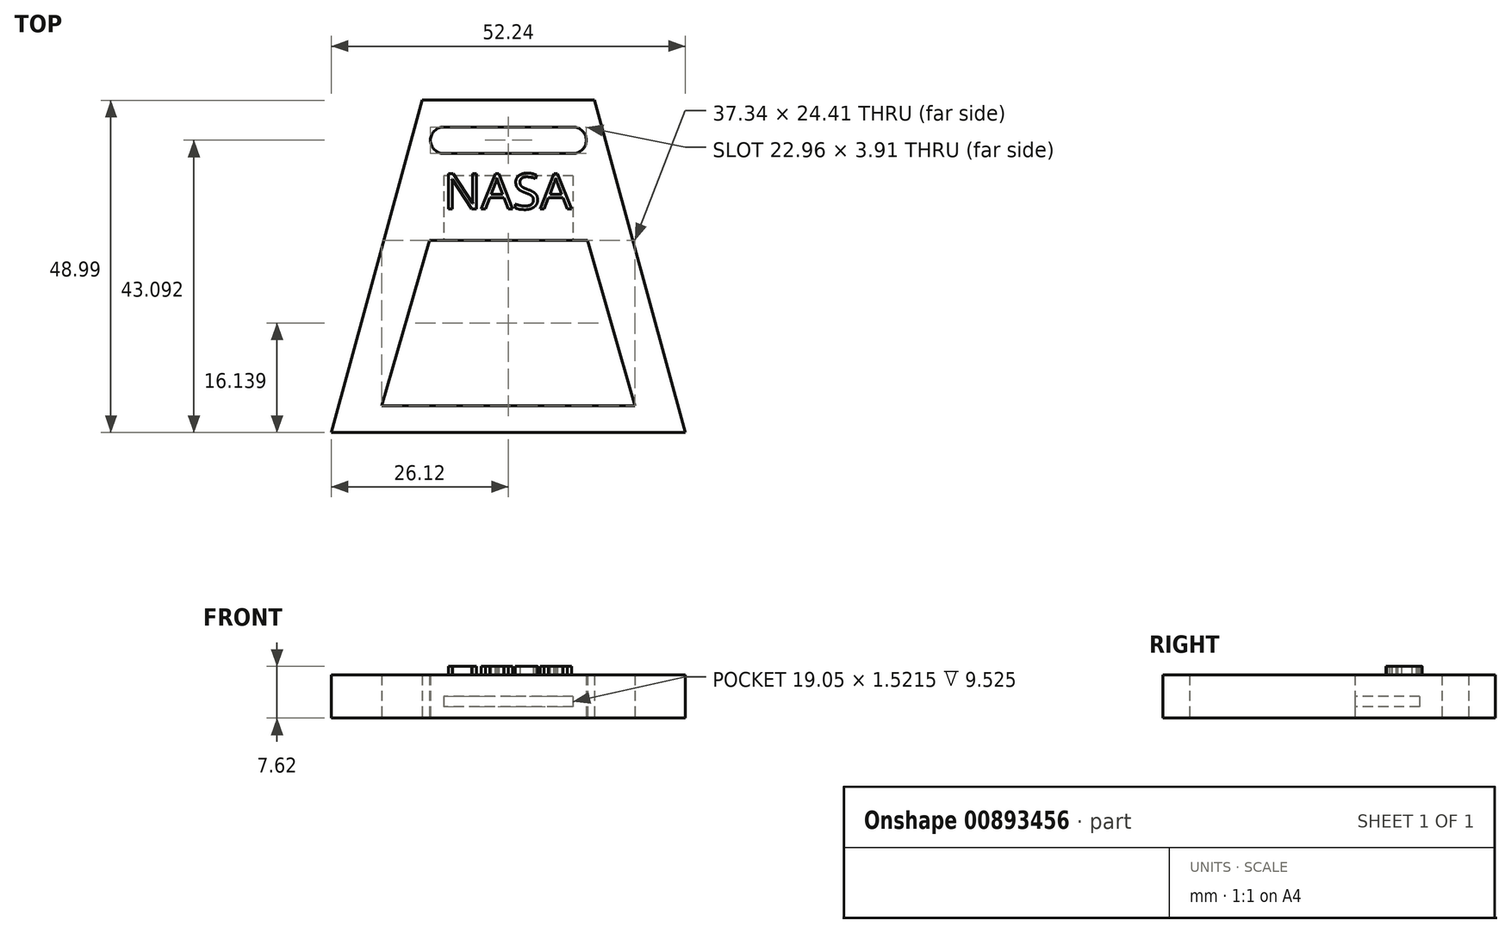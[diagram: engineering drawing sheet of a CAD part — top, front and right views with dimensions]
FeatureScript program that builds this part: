
annotation { "Feature Type Name" : "Feature", "Feature Type Description" : "" }
export const myFeature = defineFeature(function(context is Context, id is Id, definition is map)
    precondition{}
    {
        {
            var Q0;
            Q0=qCreatedBy(makeId("Top.planeOp"),FACE);
            var sketch = newSketch(context, id + "F0", { "sketchPlane" : qUnion([Q0])});
            skLineSegment(sketch, "E0", {"start": v(0, 29.12) * mm, "end": v(-12.7, 29.12) * mm});
            skLineSegment(sketch, "E1", {"start": v(-12.7, 29.12) * mm, "end": v(-26.12, -19.87) * mm});
            skLineSegment(sketch, "E2", {"start": v(-26.12, -19.87) * mm, "end": v(0, -19.87) * mm});
            skLineSegment(sketch, "E3", {"start": v(0, 25.18) * mm, "end": v(-9.53, 25.18) * mm});
            skLineSegment(sketch, "E4", {"start": v(0, 25.18) * mm, "end": v(0, 21.27) * mm});
            skLineSegment(sketch, "E5", {"start": v(0, 21.27) * mm, "end": v(-9.53, 21.27) * mm});
            skArc(sketch, "E6", {"start": v(-9.53, 25.18) * mm, "mid": v(-11.48, 23.22) * mm, "end": v(-9.53, 21.27) * mm});
            skLineSegment(sketch, "E7", {"start": v(-18.67, -15.94) * mm, "end": v(-11.66, 8.48) * mm});
            skLineSegment(sketch, "E8", {"start": v(-11.66, 8.48) * mm, "end": v(0, 8.48) * mm});
            skLineSegment(sketch, "E9", {"start": v(-11.66, 8.48) * mm, "end": v(-18.67, -15.94) * mm});
            skLineSegment(sketch, "E10", {"start": v(0, 8.48) * mm, "end": v(0, -15.94) * mm});
            skLineSegment(sketch, "E11", {"start": v(-18.67, -15.94) * mm, "end": v(0, -15.94) * mm});
            skLineSegment(sketch, "E12", {"start": v(0, -15.94) * mm, "end": v(0, -19.87) * mm});
            skLineSegment(sketch, "E13", {"start": v(0, 21.27) * mm, "end": v(0, 8.48) * mm});
            skLineSegment(sketch, "E14", {"start": v(0, 29.12) * mm, "end": v(0, 25.18) * mm});
            skSolve(sketch);
        }
        {
            var Q0;
            Q0=makeQuery(id+"F0.imprint","IMPRINT",FACE,{"disambiguationData":[TD([[makeQuery(id+"F0.imprint","IMPRINT",EDGE,{"derivedFrom":sQuery(id+"F0.wireOp",EDGE,"E0")}),1.0]])]});
            extrude(context, id + "F1", {"entities" : qUnion([Q0]), "depth" : 6.35 * mm, "offsetDistance" : 25.4 * mm});
        }
        {
            var Q0;
            Q0=makeQuery(id+"F1.opExtrude","SWEPT_FACE",FACE,{"disambiguationData":[OSD([sQuery(id+"F0.wireOp",EDGE,"E8")])]});
            var sketch = newSketch(context, id + "F2", { "sketchPlane" : qUnion([Q0])});
            skLineSegment(sketch, "E15", {"start": v(0, 1.65) * mm, "end": v(0, 3.18) * mm});
            skLineSegment(sketch, "E16", {"start": v(0, 3.18) * mm, "end": v(-9.53, 3.18) * mm});
            skLineSegment(sketch, "E17", {"start": v(0, 1.65) * mm, "end": v(-9.53, 1.65) * mm});
            skLineSegment(sketch, "E18", {"start": v(-9.53, 3.18) * mm, "end": v(-9.53, 1.65) * mm});
            skSolve(sketch);
        }
        {
            var Q0;
            Q0=makeQuery(id+"F2.imprint","IMPRINT",FACE,{"disambiguationData":[TD([[makeQuery(id+"F2.imprint","IMPRINT",EDGE,{"derivedFrom":sQuery(id+"F2.wireOp",EDGE,"E15")}),-1.0]])]});
            extrude(context, id + "F3", {"entities" : qUnion([Q0]), "operationType" : NewBodyOperationType.REMOVE, "oppositeDirection" : true, "depth" : 9.52 * mm, "offsetDistance" : 25.4 * mm});
        }
        {
            var Q0;
            Q0=makeQuery(id+"F1.opExtrude","SWEPT_BODY",BODY,{"disambiguationData":[OSD([sQuery(id+"F0.wireOp",EDGE,"E0"),sQuery(id+"F0.wireOp",EDGE,"E1"),sQuery(id+"F0.wireOp",EDGE,"E2"),sQuery(id+"F0.wireOp",EDGE,"E3"),sQuery(id+"F0.wireOp",EDGE,"E5"),sQuery(id+"F0.wireOp",EDGE,"E6"),sQuery(id+"F0.wireOp",EDGE,"E8"),sQuery(id+"F0.wireOp",EDGE,"E9"),sQuery(id+"F0.wireOp",EDGE,"E11"),sQuery(id+"F0.wireOp",EDGE,"E12"),sQuery(id+"F0.wireOp",EDGE,"E13"),sQuery(id+"F0.wireOp",EDGE,"E14")])]});
            var Q1;
            Q1=qCreatedBy(makeId("Right.planeOp"),FACE);
            mirror(context, id + "F4", {"operationType" : NewBodyOperationType.ADD, "entities" : qUnion([Q0]), "mirrorPlane" : qUnion([Q1])});
        }
        {
            var Q0;
            {var subQ0=makeQuery(id+"F1.opExtrude","CAP_FACE",FACE,{"disambiguationData":[OSD([sQuery(id+"F0.wireOp",EDGE,"E0"),sQuery(id+"F0.wireOp",EDGE,"E1"),sQuery(id+"F0.wireOp",EDGE,"E2"),sQuery(id+"F0.wireOp",EDGE,"E3"),sQuery(id+"F0.wireOp",EDGE,"E5"),sQuery(id+"F0.wireOp",EDGE,"E6"),sQuery(id+"F0.wireOp",EDGE,"E8"),sQuery(id+"F0.wireOp",EDGE,"E9"),sQuery(id+"F0.wireOp",EDGE,"E11"),sQuery(id+"F0.wireOp",EDGE,"E12"),sQuery(id+"F0.wireOp",EDGE,"E13"),sQuery(id+"F0.wireOp",EDGE,"E14")])],"isStart":false});Q0=makeQuery(id+"F4.boolean.opBoolean","MERGE",FACE,{"derivedFrom":[subQ0,makeQuery(id+"F4.opPattern","COPY",FACE,{"derivedFrom":subQ0,"instanceName":"1"})]});}
            var sketch = newSketch(context, id + "F5", { "sketchPlane" : qUnion([Q0])});
            skText(sketch, "E19", { "text": "NASA", "fontName": "OpenSans-Regular.ttf"});
            const initialGuessF5  = {"E19": [-0.00953, 0.01306, 1, 0, 0.00528]};
            skSetInitialGuess(sketch, initialGuessF5);
            skSolve(sketch);
        }
        {
            var Q0;
            Q0 = qSketchRegion(id + "F5", true);
            extrude(context, id + "F6", {"entities" : qUnion([Q0]), "operationType" : NewBodyOperationType.ADD, "depth" : 1.27 * mm, "offsetDistance" : 25.4 * mm});
        }
    });
